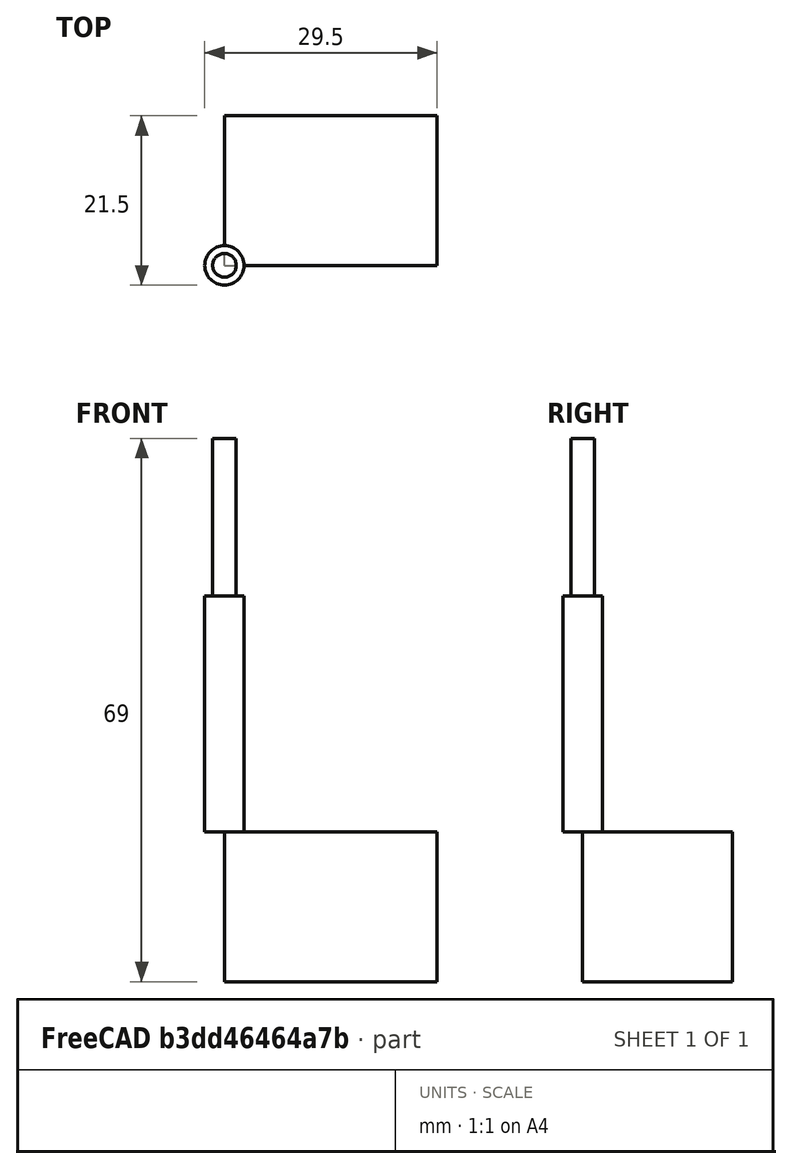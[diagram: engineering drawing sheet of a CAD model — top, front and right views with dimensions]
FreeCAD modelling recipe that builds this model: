
FCSTD DOCUMENT  (FreeCAD 0.19R23546 (Git))
Label: Adap8x17
License: All rights reserved
LicenseURL: http://en.wikipedia.org/wiki/All_rights_reserved
objects: Path::FeaturePython×4, Part::FeaturePython×3, Sketcher::SketchObject×2, PartDesign::Pad×1, PartDesign::Pocket×1, PartDesign::Body×1, App::FeaturePython×1, App::DocumentObjectGroup×1, Path::FeatureCompoundPython×1, Mesh::FeaturePython×1
note: 12 computed .brp shape members not serialized (recipe doc carries the construction recipe); baked Part::Feature solids carry a one-line shape summary decoded from their .brp

FEATURE [Sketcher::SketchObject] Sketch
  MapMode = 5
  Support = -> [XY_Plane]
  sketch-geometry (1):
    g0: Circle CenterX=0 CenterY=0 CenterZ=0 NormalX=0 NormalY=0 NormalZ=1 AngleXU=0 Radius=8.5
  constraints (2):
    c: PointOnObject(g0,g-1)
    c: Diameter(g0) = 17
FEATURE [PartDesign::Pad] Pad
  Direction = (1,1,1)
  Length = 17
  Length2 = 100
  Profile = -> Sketch
  Type = 0
FEATURE [Sketcher::SketchObject] Sketch001
  MapMode = 5
  Placement = pos=(0,0,17) rot=(0,0,1;0rad)
  Support = -> [Pad]
  sketch-geometry (1):
    g0: Circle CenterX=0 CenterY=0 CenterZ=0 NormalX=0 NormalY=0 NormalZ=1 AngleXU=0 Radius=4
  constraints (2):
    c: Coincident(g0,g-1)
    c: Diameter(g0) = 8
FEATURE [PartDesign::Pocket] Pocket
  BaseFeature = -> Pad
  Length = 5
  Length2 = 100
  Profile = -> Sketch001
  Type = 1
FEATURE [PartDesign::Body] Body
  Group = -> [Sketch,Pad,Sketch001,Pocket]
  Origin = -> Origin
  Tip = -> Pocket
FEATURE [App::FeaturePython] SetupSheet  # Path/CAM operation (typed FeaturePython)
  ClearanceHeightExpression = OpStockZMax+SetupSheet.ClearanceHeightOffset
  ClearanceHeightOffset = 5
  CoolantMode = 0
  CoolantModes = None | Flood | Mist
  FinalDepthExpression = OpFinalDepth
  HorizRapid = 0
  SafeHeightExpression = OpStockZMax+SetupSheet.SafeHeightOffset
  SafeHeightOffset = 3
  StartDepthExpression = OpStartDepth
  StepDownExpression = OpToolDiameter
  VertRapid = 0
FEATURE [Part::FeaturePython] Clone  label="Model-Body"  # Draft clone (typed FeaturePython)
  AttacherType = Attacher::AttachEngine3D
  Fuse = false
  Objects = -> [Body]
  PathResource = Model
  Placement = pos=(13.5,9.5,-18) rot=(0,0,1;0rad)
  Scale = (1,1,1)
FEATURE [App::DocumentObjectGroup] Model
  Group = -> [Clone]
FEATURE [Part::FeaturePython] ToolBit  label="Endmill"  # Path/CAM toolbit (typed FeaturePython)
  BitShape = <path>
  CuttingEdgeHeight = 30
  Diameter = 6
  Length = 50
  ShankDiameter = 3
  ShapeName = endmill
FEATURE [Path::FeaturePython] TC__Default_Tool  label="TC: Default Tool"  # Path/CAM operation (typed FeaturePython)
  HorizFeed = 0
  HorizRapid = 0
  SpindleDir = 0
  SpindleSpeed = 0
  Tool = -> ToolBit
  ToolNumber = 1
  VertFeed = 0
  VertRapid = 0
  expr: HorizRapid = SetupSheet.HorizRapid
  expr: VertRapid = SetupSheet.VertRapid
FEATURE [Part::FeaturePython] Stock  # WARN: FeaturePython — macro-defined, semantics opaque (R4)
  Base = -> Model
  ExtXneg = 5
  ExtXpos = 5
  ExtYneg = 1
  ExtYpos = 1
  ExtZneg = 1
  ExtZpos = 1
  Placement = pos=(5,1,-18) rot=(0,0,1;0rad)
  StockType = FromBase
FEATURE [Path::FeaturePython] Pocket_Shape  # Path/CAM operation (typed FeaturePython)
  Active = true
  AreaParams:
    Tolerance = 1e-07
    FitArcs = True
    Simplify = False
    CleanDistance = 0.0
    Accuracy = 0.01
    Unit = 1.0
    MinArcPoints = 4
    MaxArcPoints = 100
    ClipperScale = 10000000.0
    Fill = 0
    Coplanar = 0
    Reorient = True
    Outline = False
    Explode = False
    OpenMode = 0
    Deflection = 0.01
    SubjectFill = 0
    ClipFill = 0
    Offset = 0.0
    ExtraPass = 0
    Stepover = 0.0
    LastStepover = 0.0
    JoinType = 0
    EndType = 0
    MiterLimit = 2.0
    RoundPrecision = 0.0
    PocketMode = 2
    ToolRadius = 3.0
    PocketExtraOffset = 0.0
    PocketStepover = 6.0
    PocketLastStepover = 0.0
    FromCenter = True
    Angle = 45.0
    AngleShift = 0.0
    Shift = 0.0
    Thicken = False
    SectionCount = -1
    Stepdown = 1.0
    SectionOffset = 0.0
    SectionTolerance = 1e-06
    SectionMode = 2
    Project = False
  AttemptInverseAngle = true
  Base = -> [Clone]
  ClearanceHeight = 5
  CoolantMode = None
  CutMode = 0
  CycleTime = Erreur de temps de cycle
  EnableRotation = 0
  ExtensionCorners = true
  ExtensionLengthDefault = 3
  ExtraOffset = 0
  FinalDepth = -17
  FinishDepth = 0
  InverseAngle = false
  KeepToolDown = false
  LimitDepthToFace = true
  MinTravel = false
  OffsetPattern = 1
  OpFinalDepth = -18
  OpStartDepth = 0
  OpStockZMax = 0
  OpStockZMin = -19
  OpToolDiameter = 6
  PathParams = {'orientation': 1, 'feedrate': 0.0, 'feedrate_v': 0.0, 'verbose': True, 'resume_height': 3.0, 'retraction': 5.0, 'return_end': True, 'preamble': False}
  ReverseDirection = false
  SafeHeight = 3
  StartAt = 0
  StartDepth = 0
  StartPoint = (0,0,0)
  StepDown = 4
  StepOver = 100
  ToolController = -> TC__Default_Tool
  UseOutline = false
  UseStartPoint = false
  ZigZagAngle = 45
  expr: ExtensionLengthDefault = OpToolDiameter / 2
  expr: ClearanceHeight = OpStockZMax + SetupSheet.ClearanceHeightOffset
  expr: SafeHeight = OpStockZMax + SetupSheet.SafeHeightOffset
  expr: StepDown = 4
  expr: FinalDepth = -17
  expr: StartDepth = OpStartDepth
FEATURE [Path::FeaturePython] Profile  # Path/CAM operation (typed FeaturePython)
  Active = true
  AreaParams:
    Tolerance = 1e-07
    FitArcs = True
    Simplify = False
    CleanDistance = 0.0
    Accuracy = 0.01
    Unit = 1.0
    MinArcPoints = 4
    MaxArcPoints = 100
    ClipperScale = 10000000.0
    Fill = 0
    Coplanar = 0
    Reorient = True
    Outline = False
    Explode = False
    OpenMode = 0
    Deflection = 0.01
    SubjectFill = 0
    ClipFill = 0
    Offset = 3.0
    ExtraPass = 0
    Stepover = 0.0
    LastStepover = 0.0
    JoinType = 0
    EndType = 0
    MiterLimit = 2.0
    RoundPrecision = 0.0
    PocketMode = 0
    ToolRadius = 1.0
    PocketExtraOffset = 0.0
    PocketStepover = 0.0
    PocketLastStepover = 0.0
    FromCenter = False
    Angle = 45.0
    AngleShift = 0.0
    Shift = 0.0
    Thicken = False
    SectionCount = -1
    Stepdown = 1.0
    SectionOffset = 0.0
    SectionTolerance = 1e-06
    SectionMode = 2
    Project = False
  AttemptInverseAngle = true
  Base = -> [Clone]
  ClearanceHeight = 5
  CoolantMode = None
  CycleTime = Erreur de temps de cycle
  Direction = 0
  EnableRotation = 0
  ExpandProfile = 0
  ExpandProfileStepOver = 100
  FinalDepth = -17
  HandleMultipleFeatures = 1
  InverseAngle = false
  JoinType = 0
  LimitDepthToFace = true
  MiterLimit = 0.1
  OffsetExtra = 0
  OpFinalDepth = -18
  OpStartDepth = 0
  OpStockZMax = 0
  OpStockZMin = -19
  OpToolDiameter = 6
  PathParams = {'orientation': 1, 'feedrate': 0.0, 'feedrate_v': 0.0, 'verbose': True, 'resume_height': 3.0, 'retraction': 5.0, 'return_end': True, 'preamble': False}
  ReverseDirection = false
  SafeHeight = 3
  Side = 0
  StartDepth = 0
  StartPoint = (0,0,0)
  StepDown = 4
  ToolController = -> TC__Default_Tool
  UseComp = true
  UseStartPoint = false
  processCircles = false
  processHoles = false
  processPerimeter = true
  expr: ClearanceHeight = OpStockZMax + SetupSheet.ClearanceHeightOffset
  expr: SafeHeight = OpStockZMax + SetupSheet.SafeHeightOffset
  expr: StepDown = 4
  expr: FinalDepth = -17
  expr: StartDepth = OpStartDepth
FEATURE [Path::FeatureCompoundPython] Operations  # Path/CAM operation (typed FeaturePython)
  Group = -> [Pocket_Shape,Profile]
  UsePlacements = false
FEATURE [Path::FeaturePython] Job  # Path/CAM operation (typed FeaturePython)
  CycleTime = 00:00:00
  Fixtures = G54
  GeometryTolerance = 0.01
  LastPostProcessDate = 2021-04-23 12:38:25.923151
  LastPostProcessOutput = <userpath>/Dev/CNC/MiscCNC/Adap8x17.gcode
  Model = -> Model
  Operations = -> Operations
  OrderOutputBy = 0
  PostProcessor = 13
  PostProcessorOutputFile = <userpath>/Dev/CNC/MiscCNC/Adap8x17.gcode
  SetupSheet = -> SetupSheet
  SplitOutput = false
  Stock = -> Stock
  ToolController = -> [TC__Default_Tool]
FEATURE [Mesh::FeaturePython] CutMaterial  # WARN: FeaturePython — macro-defined, semantics opaque (R4)
note: 1 file-system path scrubbed to <path> (originals preserved in the JSON sidecar)
